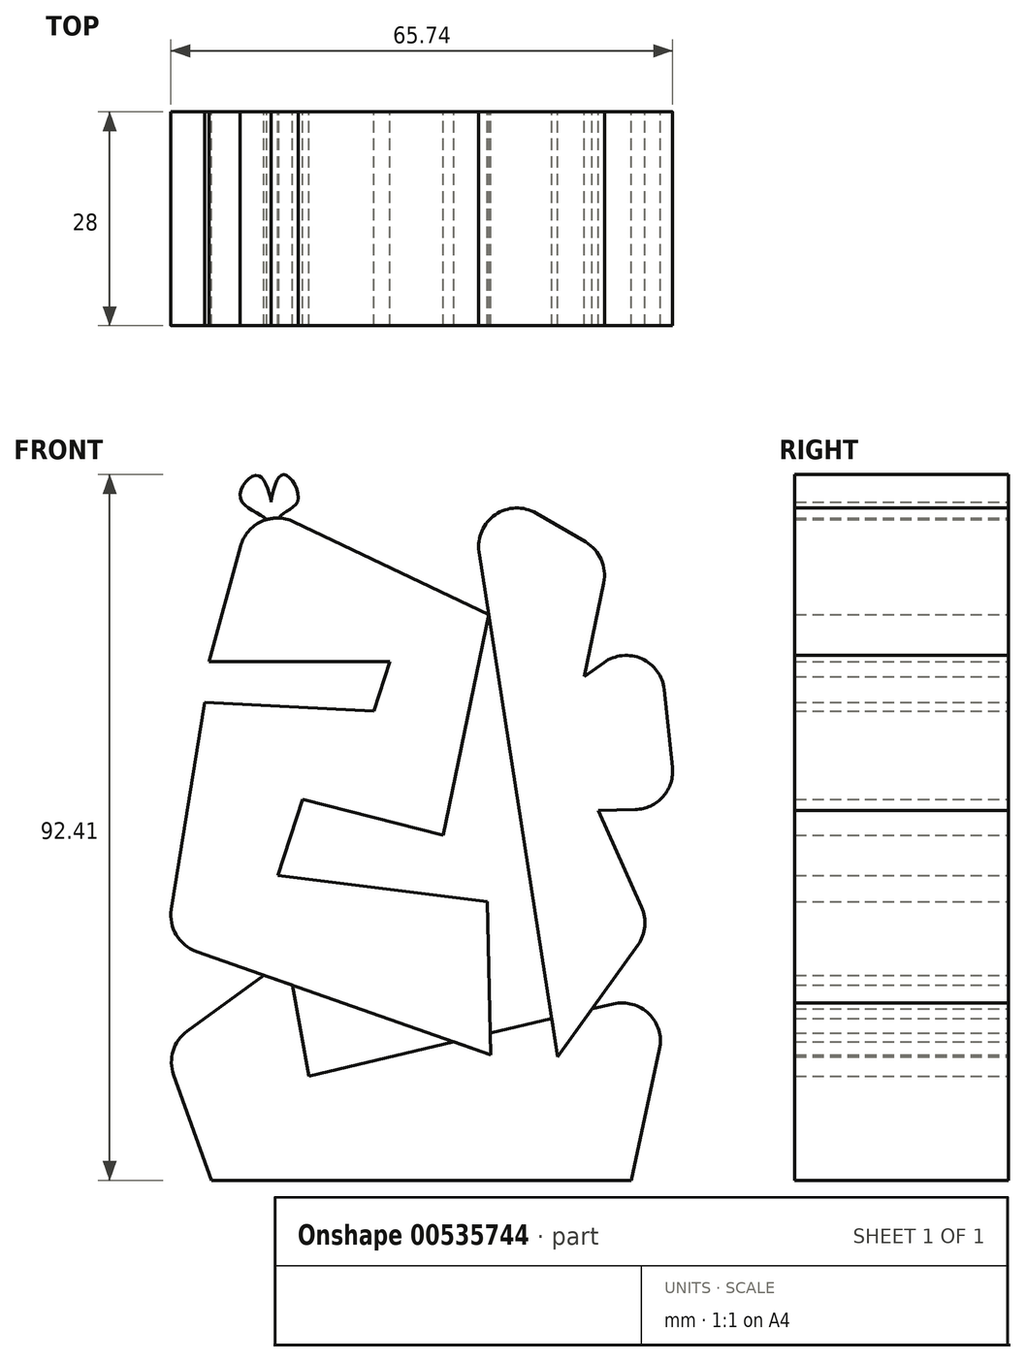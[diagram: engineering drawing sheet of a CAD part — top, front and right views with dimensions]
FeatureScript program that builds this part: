
annotation { "Feature Type Name" : "Feature", "Feature Type Description" : "" }
export const myFeature = defineFeature(function(context is Context, id is Id, definition is map)
    precondition{}
    {
        {
            var Q0;
            Q0=qCreatedBy(makeId("Front.planeOp"),FACE);
            var sketch = newSketch(context, id + "F0", { "sketchPlane" : qUnion([Q0])});
            skLineSegment(sketch, "E0", {"start": v(-19.55, 33.54) * mm, "end": v(6, 21.38) * mm});
            skLineSegment(sketch, "E1", {"start": v(6, 21.38) * mm, "end": v(0, -7.53) * mm});
            skLineSegment(sketch, "E2", {"start": v(0, -7.53) * mm, "end": v(-18.41, -2.83) * mm});
            skLineSegment(sketch, "E3", {"start": v(-18.41, -2.83) * mm, "end": v(-21.65, -12.77) * mm});
            skLineSegment(sketch, "E4", {"start": v(-21.65, -12.77) * mm, "end": v(5.8, -16.17) * mm});
            skLineSegment(sketch, "E5", {"start": v(5.8, -16.17) * mm, "end": v(6.23, -36.26) * mm});
            skLineSegment(sketch, "E6", {"start": v(6.23, -36.26) * mm, "end": v(-32.32, -22.71) * mm});
            skLineSegment(sketch, "E7", {"start": v(-35.6, -17.2) * mm, "end": v(-31.21, 9.87) * mm});
            skLineSegment(sketch, "E8", {"start": v(-31.21, 9.87) * mm, "end": v(-9.06, 8.78) * mm});
            skLineSegment(sketch, "E9", {"start": v(-9.06, 8.78) * mm, "end": v(-7, 15.25) * mm});
            skLineSegment(sketch, "E10", {"start": v(-7, 15.25) * mm, "end": v(-30.68, 15.25) * mm});
            skLineSegment(sketch, "E11", {"start": v(-30.68, 15.25) * mm, "end": v(-26.52, 30.36) * mm});
            skLineSegment(sketch, "E12", {"start": v(4.73, 29.57) * mm, "end": v(15.01, -36.54) * mm});
            skLineSegment(sketch, "E13", {"start": v(15.01, -36.54) * mm, "end": v(25.52, -21.88) * mm});
            skLineSegment(sketch, "E14", {"start": v(26.02, -16.92) * mm, "end": v(20.34, -4.25) * mm});
            skLineSegment(sketch, "E15", {"start": v(20.34, -4.25) * mm, "end": v(25.18, -4.14) * mm});
            skLineSegment(sketch, "E16", {"start": v(30.05, 1.39) * mm, "end": v(28.96, 11.58) * mm});
            skLineSegment(sketch, "E17", {"start": v(21.07, 15.1) * mm, "end": v(18.5, 13.26) * mm});
            skLineSegment(sketch, "E18", {"start": v(18.5, 13.26) * mm, "end": v(21.05, 25.55) * mm});
            skLineSegment(sketch, "E19", {"start": v(18.67, 30.89) * mm, "end": v(12.18, 34.66) * mm});
            skLineSegment(sketch, "E20", {"start": v(-33.53, -33.17) * mm, "end": v(-20.34, -23.55) * mm});
            skLineSegment(sketch, "E21", {"start": v(-20.34, -23.55) * mm, "end": v(-17.56, -39.1) * mm});
            skLineSegment(sketch, "E22", {"start": v(-17.56, -39.1) * mm, "end": v(22.3, -29.6) * mm});
            skLineSegment(sketch, "E23", {"start": v(28.35, -35.52) * mm, "end": v(24.64, -52.69) * mm});
            skLineSegment(sketch, "E24", {"start": v(24.64, -52.69) * mm, "end": v(-30.31, -52.69) * mm});
            skLineSegment(sketch, "E25", {"start": v(-30.31, -52.69) * mm, "end": v(-35.28, -38.9) * mm});
            skPoint(sketch, "E26", {"position": v(6.23, -33.43) * mm});
            skPoint(sketch, "E27.visualSharp", {"position": v(-24.94, 36.1) * mm});
            skArc(sketch, "E27.filletArc", {"start": v(-19.55, 33.54) * mm, "mid": v(-23.78, 33.58) * mm, "end": v(-26.52, 30.36) * mm});
            skPoint(sketch, "E28.visualSharp", {"position": v(3.12, 39.94) * mm});
            skArc(sketch, "E28.filletArc", {"start": v(12.18, 34.66) * mm, "mid": v(6.85, 34.47) * mm, "end": v(4.73, 29.57) * mm});
            skPoint(sketch, "E29.visualSharp", {"position": v(28.04, 20.11) * mm});
            skArc(sketch, "E29.filletArc", {"start": v(28.96, 11.58) * mm, "mid": v(26.03, 15.6) * mm, "end": v(21.07, 15.1) * mm});
            skPoint(sketch, "E30.visualSharp", {"position": v(21.79, 29.07) * mm});
            skArc(sketch, "E30.filletArc", {"start": v(21.05, 25.55) * mm, "mid": v(20.72, 28.6) * mm, "end": v(18.67, 30.89) * mm});
            skPoint(sketch, "E31.visualSharp", {"position": v(30.63, -4.03) * mm});
            skArc(sketch, "E31.filletArc", {"start": v(25.18, -4.14) * mm, "mid": v(28.83, -2.45) * mm, "end": v(30.05, 1.39) * mm});
            skPoint(sketch, "E32.visualSharp", {"position": v(27.2, -19.55) * mm});
            skArc(sketch, "E32.filletArc", {"start": v(25.52, -21.88) * mm, "mid": v(26.43, -19.47) * mm, "end": v(26.02, -16.92) * mm});
            skPoint(sketch, "E33.visualSharp", {"position": v(-36.27, -21.33) * mm});
            skArc(sketch, "E33.filletArc", {"start": v(-35.6, -17.2) * mm, "mid": v(-34.96, -20.55) * mm, "end": v(-32.32, -22.71) * mm});
            skPoint(sketch, "E34.visualSharp", {"position": v(-36.55, -35.38) * mm});
            skArc(sketch, "E34.filletArc", {"start": v(-33.53, -33.17) * mm, "mid": v(-35.36, -35.75) * mm, "end": v(-35.28, -38.9) * mm});
            skPoint(sketch, "E35.visualSharp", {"position": v(30.03, -27.76) * mm});
            skArc(sketch, "E35.filletArc", {"start": v(28.35, -35.52) * mm, "mid": v(26.96, -30.9) * mm, "end": v(22.3, -29.6) * mm});
            skFitSpline(sketch, "E36", {"points": [v(-23.13, 33.82) * mm, v(-26.54, 36.63) * mm, v(-24.4, 39.63) * mm, v(-22.5, 36.12) * mm, v(-22.36, 33.99) * mm], "startDerivative": vector(-8.05, 8.98) * mm, "endDerivative": vector(-0.5, -8.15) * mm});
            skFitSpline(sketch, "E37", {"points": [v(-22.36, 33.99) * mm, v(-22.5, 36.12) * mm, v(-20.9, 39.72) * mm, v(-19, 36.36) * mm, v(-21.5, 34.03) * mm], "startDerivative": vector(-1.79, 7.89) * mm, "endDerivative": vector(-5.42, -9.94) * mm});
            skSolve(sketch);
        }
        {
            var Q0;
            Q0=makeQuery(id+"F0.imprint","IMPRINT",FACE,{"disambiguationData":[TD([[makeQuery(id+"F0.imprint","IMPRINT",EDGE,{"derivedFrom":sQuery(id+"F0.wireOp",EDGE,"E0")}),-1.0]])]});
            var Q1;
            Q1=makeQuery(id+"F0.imprint","IMPRINT",FACE,{"disambiguationData":[TD([[makeQuery(id+"F0.imprint","IMPRINT",EDGE,{"derivedFrom":sQuery(id+"F0.wireOp",EDGE,"E14")}),1.0]])]});
            var Q2;
            {var subQ0=sQuery(id+"F0.wireOp",EDGE,"E20");var subQ1=sQuery(id+"F0.wireOp",EDGE,"E6");var subQ2=makeQuery(id+"F0.imprint","INTERSECT",VERTEX,{"derivedFrom":[subQ1,subQ0]});Q2=makeQuery(id+"F0.imprint","IMPRINT",FACE,{"disambiguationData":[TD([[makeQuery(id+"F0.imprint","IMPRINT",EDGE,{"disambiguationData":[TD([[subQ2,1.0]])],"derivedFrom":subQ1}),-1.0]])]});}
            var Q3;
            {var subQ0=sQuery(id+"F0.wireOp",EDGE,"E6");var subQ1=sQuery(id+"F0.wireOp",EDGE,"E5");var subQ2=makeQuery(id+"F0.imprint","INTERSECT",VERTEX,{"derivedFrom":[subQ1,subQ0]});Q3=makeQuery(id+"F0.imprint","IMPRINT",FACE,{"disambiguationData":[TD([[makeQuery(id+"F0.imprint","IMPRINT",EDGE,{"disambiguationData":[TD([[subQ2,1.0]])],"derivedFrom":subQ1}),-1.0]])]});}
            var Q4;
            {var subQ0=sQuery(id+"F0.wireOp",EDGE,"E13");var subQ1=sQuery(id+"F0.wireOp",EDGE,"E12");var subQ2=makeQuery(id+"F0.imprint","INTERSECT",VERTEX,{"derivedFrom":[subQ1,subQ0]});Q4=makeQuery(id+"F0.imprint","IMPRINT",FACE,{"disambiguationData":[TD([[makeQuery(id+"F0.imprint","IMPRINT",EDGE,{"disambiguationData":[TD([[subQ2,1.0]])],"derivedFrom":subQ1}),1.0]])]});}
            extrude(context, id + "F1", {"entities" : qUnion([Q0, Q1, Q2, Q3, Q4]), "depth" : 28 * mm, "offsetDistance" : 25 * mm});
        }
        {
            var Q0;
            {var subQ0=sQuery(id+"F0.wireOp",EDGE,"E36");var subQ1=sQuery(id+"F0.wireOp",EDGE,"E27.filletArc");var subQ2=makeQuery(id+"F0.imprint","INTERSECT",VERTEX,{"derivedFrom":[subQ1,subQ0]});Q0=makeQuery(id+"F0.imprint","IMPRINT",FACE,{"disambiguationData":[TD([[makeQuery(id+"F0.imprint","IMPRINT",EDGE,{"disambiguationData":[TD([[subQ2,-1.0]])],"derivedFrom":subQ0}),-1.0]])]});}
            var Q1;
            {var subQ0=sQuery(id+"F0.wireOp",EDGE,"E37");var subQ2=sQuery(id+"F0.wireOp",EDGE,"E27.filletArc");var subQ4=makeQuery(id+"F0.imprint","INTERSECT",VERTEX,{"derivedFrom":[subQ2,subQ0]});Q1=makeQuery(id+"F0.imprint","IMPRINT",FACE,{"disambiguationData":[TD([[makeQuery(id+"F0.imprint","IMPRINT",EDGE,{"disambiguationData":[TD([[subQ4,1.0]])],"derivedFrom":subQ0}),-1.0]])]});}
            var Q2;
            {var subQ0=sQuery(id+"F0.wireOp",EDGE,"E37");var subQ1=sQuery(id+"F0.wireOp",EDGE,"E36");var subQ3=makeQuery(id+"F0.imprint","INTERSECT",VERTEX,{"derivedFrom":[subQ1,subQ0]});Q2=makeQuery(id+"F0.imprint","IMPRINT",FACE,{"disambiguationData":[TD([[makeQuery(id+"F0.imprint","IMPRINT",EDGE,{"disambiguationData":[TD([[subQ3,-1.0]])],"derivedFrom":subQ1}),-1.0]])]});}
            var Q3;
            Q3=makeQuery(id+"F0.imprint","IMPRINT",FACE,{"disambiguationData":[TD([[makeQuery(id+"F0.imprint","IMPRINT",EDGE,{"derivedFrom":sQuery(id+"F0.wireOp",EDGE,"E23")}),-1.0]])]});
            extrude(context, id + "F2", {"entities" : qUnion([Q0, Q1, Q2, Q3]), "depth" : 28 * mm, "offsetDistance" : 25 * mm});
        }
    });
